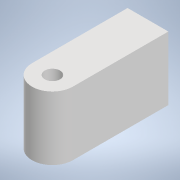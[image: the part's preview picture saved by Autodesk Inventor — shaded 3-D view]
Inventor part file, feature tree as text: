
AUTODESK INVENTOR PART (.ipt)
format: ipt  version: 2022 (Build 260153000, 153)  size: 96,768 bytes
history: native  units: mm
features: extrude x1, sketch x1
ambient origin geometry x8: Origin, YZ Plane, XZ Plane, XY Plane, X Axis, Y Axis, Z Axis, Center Point
bodies: Solid1 (feature_tree)
feature tree (2):
  extrude  "Extrusion1"  Depth=10.0mm
  sketch  "Sketch1"  dims[d0=2.4mm d1=2.0mm d2=15.0mm d3=10.0mm d4=0.0mm]
